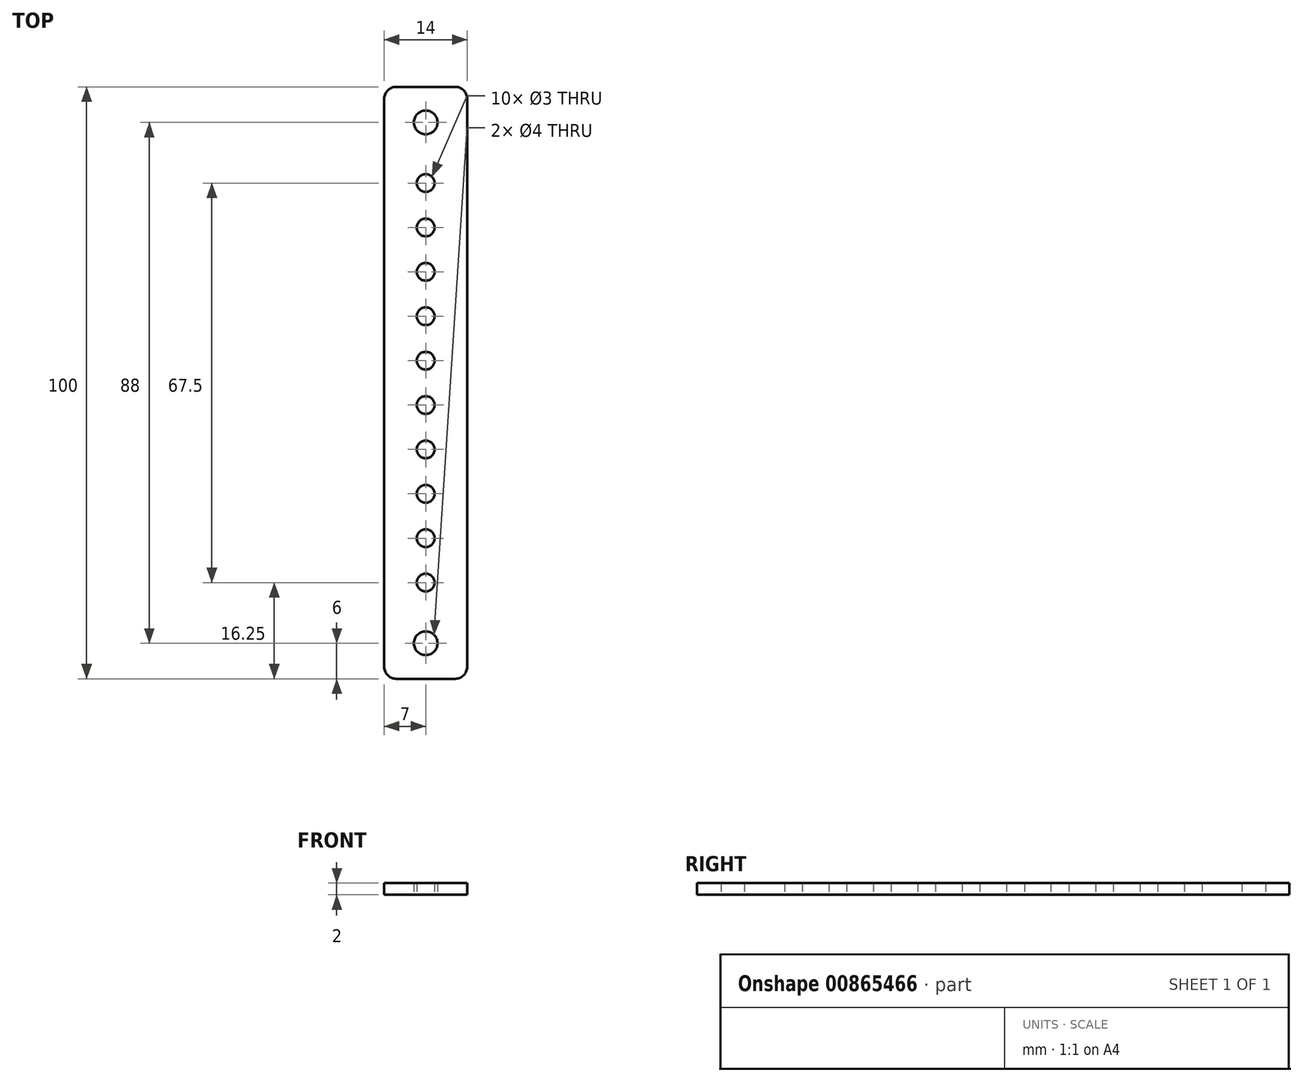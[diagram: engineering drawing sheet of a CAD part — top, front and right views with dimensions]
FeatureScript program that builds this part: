
annotation { "Feature Type Name" : "Feature", "Feature Type Description" : "" }
export const myFeature = defineFeature(function(context is Context, id is Id, definition is map)
    precondition{}
    {
        {
            var Q0;
            Q0=qCreatedBy(makeId("Top.planeOp"),FACE);
            var sketch = newSketch(context, id + "F0", { "sketchPlane" : qUnion([Q0])});
            skLineSegment(sketch, "E0.bottom", {"start": v(5, 50) * mm, "end": v(-5, 50) * mm});
            skLineSegment(sketch, "E0.top", {"start": v(5, -50) * mm, "end": v(-5, -50) * mm});
            skLineSegment(sketch, "E0.left", {"start": v(7, 48) * mm, "end": v(7, -48) * mm});
            skLineSegment(sketch, "E0.right", {"start": v(-7, 48) * mm, "end": v(-7, -48) * mm});
            skPoint(sketch, "E0.middle", {"position": v(0, 0) * mm});
            skPoint(sketch, "E1.visualSharp", {"position": v(-7, 50) * mm});
            skArc(sketch, "E1.filletArc", {"start": v(-5, 50) * mm, "mid": v(-6.41, 49.41) * mm, "end": v(-7, 48) * mm});
            skPoint(sketch, "E2.visualSharp", {"position": v(-7, -50) * mm});
            skArc(sketch, "E2.filletArc", {"start": v(-7, -48) * mm, "mid": v(-6.41, -49.41) * mm, "end": v(-5, -50) * mm});
            skPoint(sketch, "E3.visualSharp", {"position": v(7, -50) * mm});
            skArc(sketch, "E3.filletArc", {"start": v(5, -50) * mm, "mid": v(6.41, -49.41) * mm, "end": v(7, -48) * mm});
            skPoint(sketch, "E4.visualSharp", {"position": v(7, 50) * mm});
            skArc(sketch, "E4.filletArc", {"start": v(7, 48) * mm, "mid": v(6.41, 49.41) * mm, "end": v(5, 50) * mm});
            skPoint(sketch, "E5.center.orphan", {"position": v(-5.5, 0) * mm});
            skPoint(sketch, "E6.center.orphan", {"position": v(5.5, 0) * mm});
            skCircle(sketch, "E7", {"center": v(0, 44) * mm, "radius": 2 * mm});
            skCircle(sketch, "E8", {"center": v(0, -44) * mm, "radius": 2 * mm});
            skPoint(sketch, "E8.centerSnap0", {"position": v(0, 50) * mm});
            skCircle(sketch, "E9", {"center": v(0, 33.75) * mm, "radius": 1.5 * mm});
            skCircle(sketch, "E10.0.1.0", {"center": v(0, 26.25) * mm, "radius": 1.5 * mm});
            skCircle(sketch, "E10.0.2.0", {"center": v(0, 18.75) * mm, "radius": 1.5 * mm});
            skCircle(sketch, "E10.0.3.0", {"center": v(0, 11.25) * mm, "radius": 1.5 * mm});
            skCircle(sketch, "E10.0.4.0", {"center": v(0, 3.75) * mm, "radius": 1.5 * mm});
            skLineSegment(sketch, "E10.direction1", {"start": v(0, 33.75) * mm, "end": v(25, 33.75) * mm, "construction": true});
            skLineSegment(sketch, "E10.direction2", {"start": v(0, 33.75) * mm, "end": v(0, 26.25) * mm, "construction": true});
            skCircle(sketch, "E11.0.0.5", {"center": v(0, -3.75) * mm, "radius": 1.5 * mm});
            skCircle(sketch, "E11.0.0.6", {"center": v(0, -11.25) * mm, "radius": 1.5 * mm});
            skCircle(sketch, "E11.0.0.7", {"center": v(0, -18.75) * mm, "radius": 1.5 * mm});
            skCircle(sketch, "E11.0.0.8", {"center": v(0, -26.25) * mm, "radius": 1.5 * mm});
            skCircle(sketch, "E11.0.0.9", {"center": v(0, -33.75) * mm, "radius": 1.5 * mm});
            skSolve(sketch);
        }
        {
            var Q0;
            Q0=qSketchRegion(id+"F0",true);
            extrude(context, id + "F1", {"entities" : qUnion([Q0]), "depth" : 2 * mm, "offsetDistance" : 25 * mm});
        }
    });
